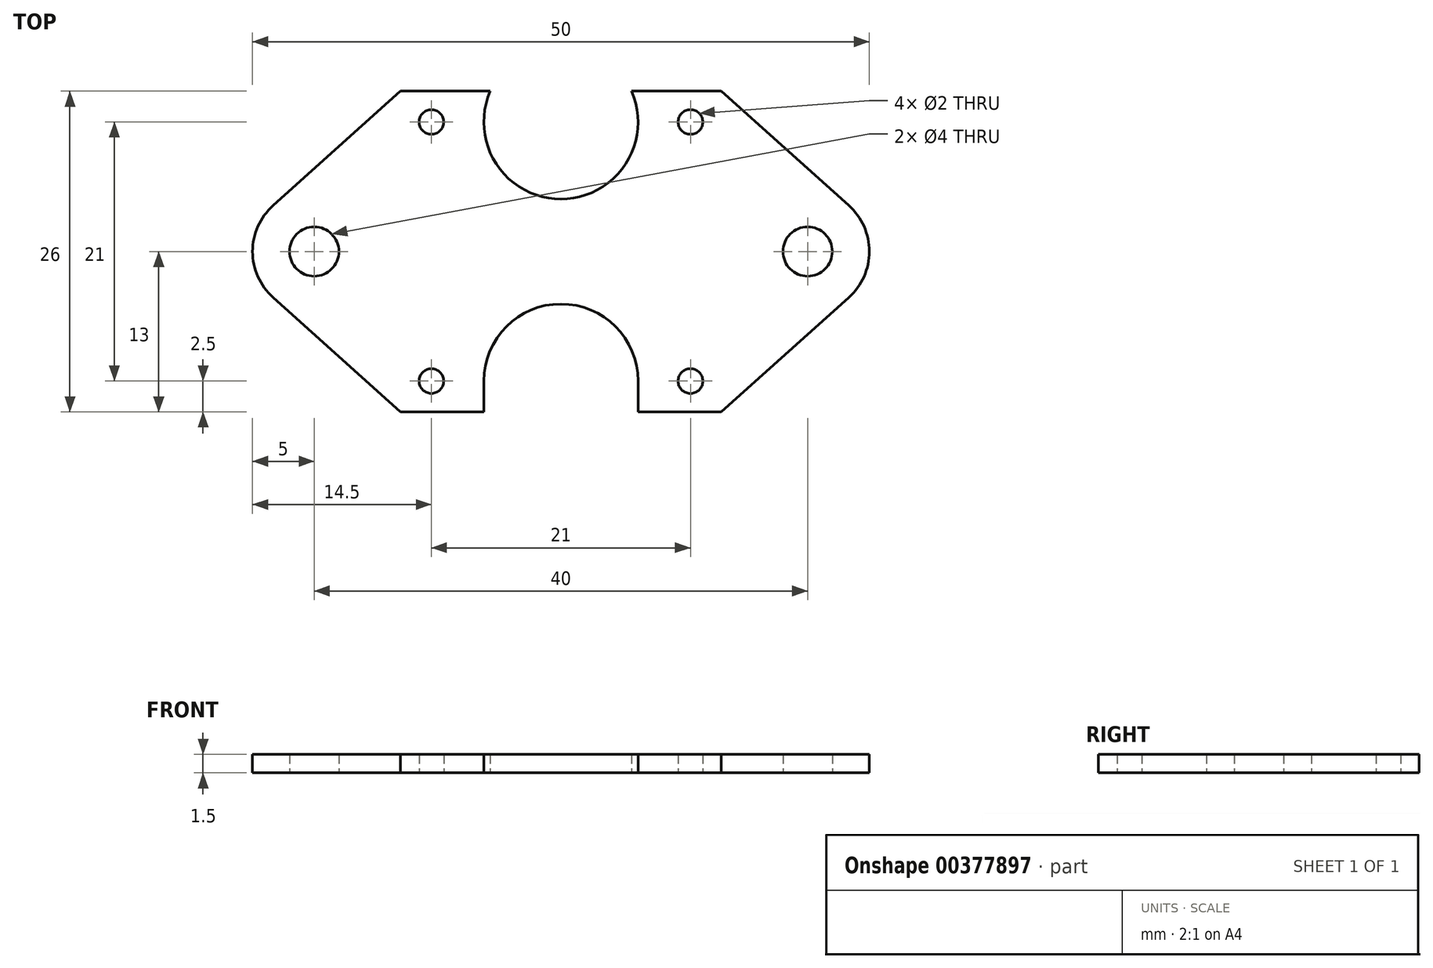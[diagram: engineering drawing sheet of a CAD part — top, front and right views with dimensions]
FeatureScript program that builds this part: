
annotation { "Feature Type Name" : "Feature", "Feature Type Description" : "" }
export const myFeature = defineFeature(function(context is Context, id is Id, definition is map)
    precondition{}
    {
        {
            var Q0;
            Q0=qCreatedBy(makeId("Top.planeOp"),FACE);
            var sketch = newSketch(context, id + "F0", { "sketchPlane" : qUnion([Q0])});
            skLineSegment(sketch, "E0.bottom", {"start": v(-13, 13) * mm, "end": v(13, 13) * mm});
            skLineSegment(sketch, "E0.top", {"start": v(-13, -13) * mm, "end": v(13, -13) * mm});
            skLineSegment(sketch, "E0.left", {"start": v(-13, 13) * mm, "end": v(-13, -13) * mm});
            skLineSegment(sketch, "E0.right", {"start": v(13, 13) * mm, "end": v(13, -13) * mm});
            skPoint(sketch, "E0.middle", {"position": v(0, 0) * mm});
            skLineSegment(sketch, "E1.bottom", {"start": v(-10.5, 10.5) * mm, "end": v(10.5, 10.5) * mm, "construction": true});
            skLineSegment(sketch, "E1.top", {"start": v(-10.5, -10.5) * mm, "end": v(10.5, -10.5) * mm, "construction": true});
            skLineSegment(sketch, "E1.left", {"start": v(-10.5, 10.5) * mm, "end": v(-10.5, -10.5) * mm, "construction": true});
            skLineSegment(sketch, "E1.right", {"start": v(10.5, 10.5) * mm, "end": v(10.5, -10.5) * mm, "construction": true});
            skCircle(sketch, "E2", {"center": v(-10.5, -10.5) * mm, "radius": 1 * mm});
            skCircle(sketch, "E3.MirrorC", {"center": v(10.5, -10.5) * mm, "radius": 1 * mm});
            skCircle(sketch, "E4.MirrorC", {"center": v(-10.5, 10.5) * mm, "radius": 1 * mm});
            skCircle(sketch, "E5.MirrorC", {"center": v(10.5, 10.5) * mm, "radius": 1 * mm});
            skCircle(sketch, "E6", {"center": v(0, 25.5) * mm, "radius": 2 * mm});
            skArc(sketch, "E7", {"start": v(4.33, 28) * mm, "mid": v(0, 30.5) * mm, "end": v(-4.33, 28) * mm});
            skLineSegment(sketch, "E8", {"start": v(-13, 13) * mm, "end": v(-4.33, 28) * mm});
            skLineSegment(sketch, "E9.MirrorCS", {"start": v(13, 13) * mm, "end": v(4.33, 28) * mm});
            skArc(sketch, "E10", {"start": v(-5.73, -13) * mm, "mid": v(0, -16.75) * mm, "end": v(5.73, -13) * mm, "construction": true});
            skLineSegment(sketch, "E11", {"start": v(-6.25, -10.5) * mm, "end": v(-6.25, -13) * mm});
            skArc(sketch, "E12.trimOffspring", {"start": v(6.25, -10.5) * mm, "mid": v(0, -4.25) * mm, "end": v(-6.25, -10.5) * mm});
            skLineSegment(sketch, "E13.MirrorCS", {"start": v(6.25, -10.5) * mm, "end": v(6.25, -13) * mm});
            skCircle(sketch, "E14", {"center": v(-20, 0) * mm, "radius": 2 * mm});
            skArc(sketch, "E15", {"start": v(-23.34, 3.72) * mm, "mid": v(-25, 0) * mm, "end": v(-23.34, -3.72) * mm});
            skLineSegment(sketch, "E16", {"start": v(-13, 13) * mm, "end": v(-23.34, 3.72) * mm});
            skLineSegment(sketch, "E17.MirrorCS", {"start": v(-13, -13) * mm, "end": v(-23.34, -3.72) * mm});
            skLineSegment(sketch, "E18.MirrorCS", {"start": v(13, 13) * mm, "end": v(23.34, 3.72) * mm});
            skArc(sketch, "E19.MirrorCS", {"start": v(23.34, 3.72) * mm, "mid": v(25, 0) * mm, "end": v(23.34, -3.72) * mm});
            skCircle(sketch, "E20.MirrorC", {"center": v(20, 0) * mm, "radius": 2 * mm});
            skLineSegment(sketch, "E21.MirrorCS", {"start": v(13, -13) * mm, "end": v(23.34, -3.72) * mm});
            skCircle(sketch, "E22", {"center": v(0, 10.5) * mm, "radius": 6.25 * mm});
            skSolve(sketch);
        }
        {
            var Q0;
            Q0=makeQuery(id+"F0.imprint","IMPRINT",FACE,{"disambiguationData":[TD([[makeQuery(id+"F0.imprint","IMPRINT",EDGE,{"derivedFrom":sQuery(id+"F0.wireOp",EDGE,"E0.left")}),-1.0]])]});
            var Q1;
            Q1=makeQuery(id+"F0.imprint","IMPRINT",FACE,{"disambiguationData":[TD([[makeQuery(id+"F0.imprint","IMPRINT",EDGE,{"derivedFrom":sQuery(id+"F0.wireOp",EDGE,"E0.right")}),1.0]])]});
            var Q2;
            {var subQ1=sQuery(id+"F0.wireOp",EDGE,"E0.left");Q2=makeQuery(id+"F0.imprint","IMPRINT",FACE,{"disambiguationData":[TD([[makeQuery(id+"F0.imprint","IMPRINT",EDGE,{"derivedFrom":subQ1}),1.0]])]});}
            var Q3;
            {var subQ0=sQuery(id+"F0.wireOp",EDGE,"E22");var subQ1=sQuery(id+"F0.wireOp",EDGE,"E0.bottom");var subQ2=makeQuery(id+"F0.imprint","INTERSECT",VERTEX,{"disambiguationData":[OD(0.0)],"derivedFrom":[subQ1,subQ0]});Q3=makeQuery(id+"F0.imprint","IMPRINT",FACE,{"disambiguationData":[TD([[makeQuery(id+"F0.imprint","IMPRINT",EDGE,{"disambiguationData":[TD([[subQ2,-1.0]])],"derivedFrom":subQ1}),-1.0]])]});}
            extrude(context, id + "F1", {"entities" : qUnion([Q0, Q1, Q2, Q3]), "depth" : 1.5 * mm});
        }
    });
